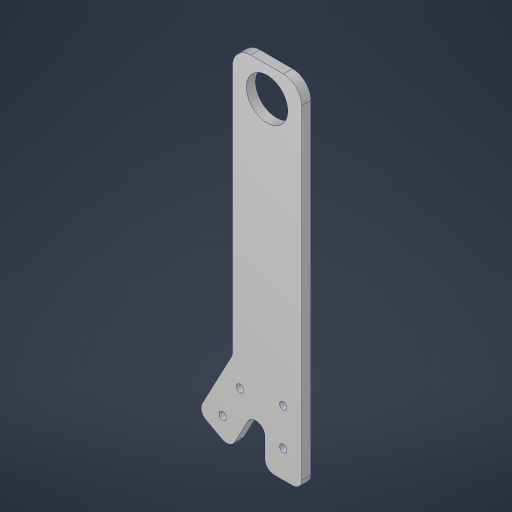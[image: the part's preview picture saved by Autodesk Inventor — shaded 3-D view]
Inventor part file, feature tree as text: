
AUTODESK INVENTOR PART (.ipt)
format: ipt  version: 2023.4 (Build 274418000, 418)  size: 243,712 bytes
history: native  units: in
note: dims shown in document units (in); Inventor stores cm internally (conversion verified against a paired STEP export)
features: projected_geometry x3, sketch x2, extrude x2, hole x2, fillet x2
ambient origin geometry x8: Origin, YZ Plane, XZ Plane, XY Plane, X Axis, Y Axis, Z Axis, Center Point
bodies: Solid1 (feature_tree)
feature tree (11):
  sketch  "Sketch1"  dims[d0=1.0in d1=1.0in]
  extrude  "Extrusion1"  Depth=1.0in
  hole  "Hole1"  [1 undecoded]
  sketch  "Sketch2"  dims[d2=0.1924in d3=2.0in d4=1.0in d5=0.5in d6=1.0in d7=0.5in d8=2.25in d9=0.25in d10=0.0in d11=0.201in d12=0.75in d13=0.385in d14=0.25in d15=0.5635in d16=1.0in d17=0.8108in d18=0.25in d19=1.125in d20=6.5in d22=1.0in d23=0.0in d24=1.125in d25=0.75in d26=0.385in d27=0.25in d28=0.5635in d29=1.0in d30=0.8108in d31=0.5in d32=0.25in d36=0.0in d37=0.25in d38=0.25in]
  extrude  "Extrusion2"  Depth=1.0in
  fillet  "Fillet1"  Radius=0.5in
  hole  "Hole2"  [1 undecoded]
  fillet  "Fillet2"  Radius=0.5in
  projected_geometry  "Projected Loop1"
  projected_geometry  "Project Cut Edges1"
  projected_geometry  "Project Cut Edges2"
note: 2 required parameter values undecoded (feature->parameter linkage not recoverable at this tier; creation-order binding heuristic only, values carry confidence <= 0.55)
